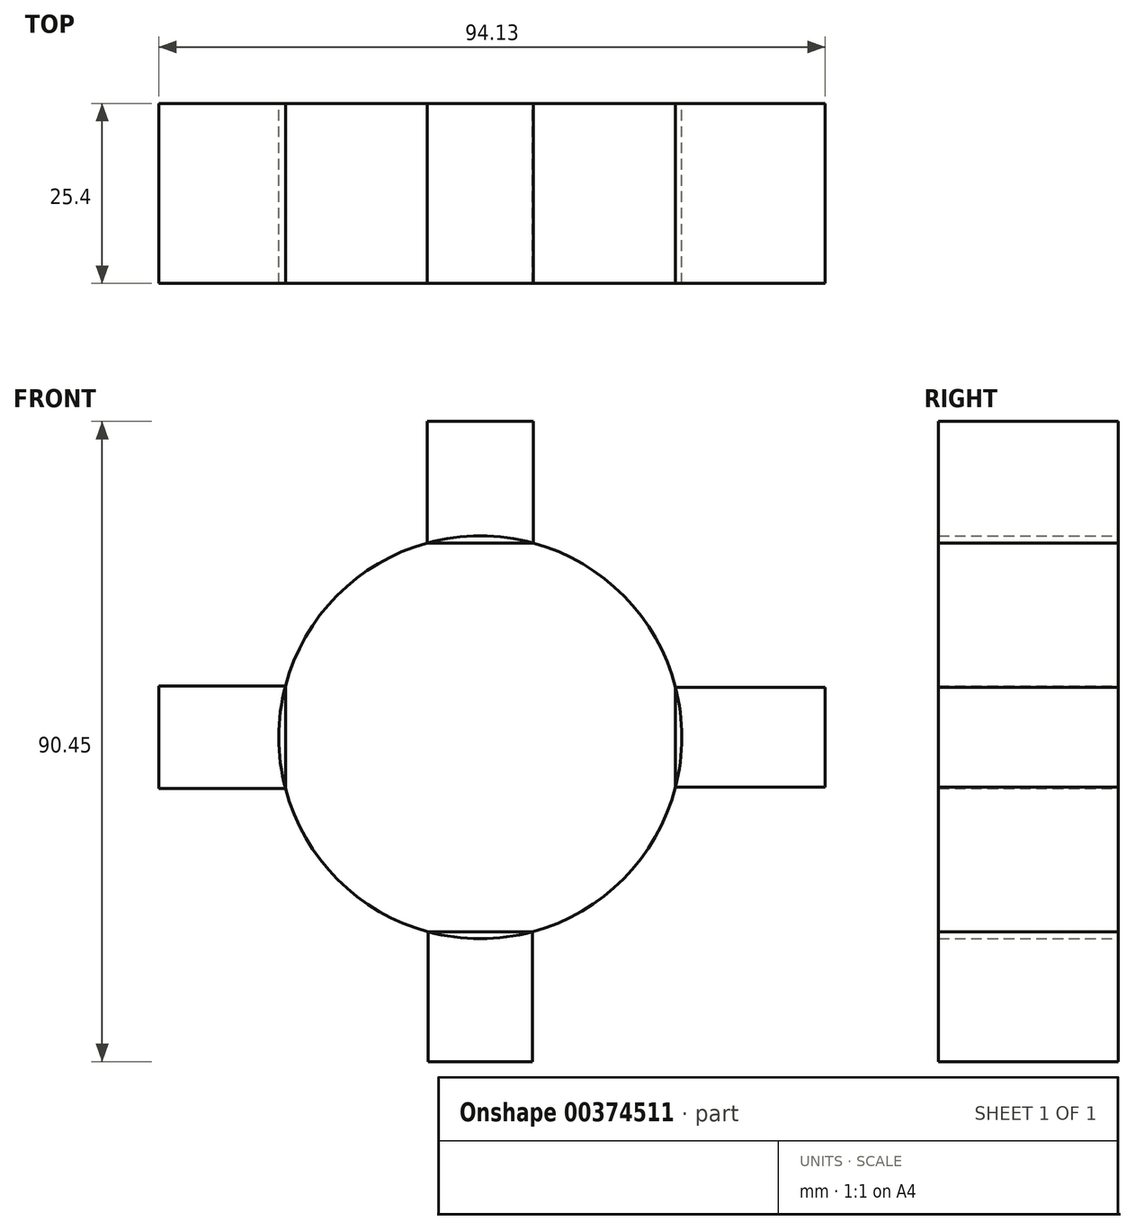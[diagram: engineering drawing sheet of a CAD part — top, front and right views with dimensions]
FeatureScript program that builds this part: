
annotation { "Feature Type Name" : "Feature", "Feature Type Description" : "" }
export const myFeature = defineFeature(function(context is Context, id is Id, definition is map)
    precondition{}
    {
        {
            var Q0;
            Q0=qCreatedBy(makeId("Front.planeOp"),FACE);
            var sketch = newSketch(context, id + "F0", { "sketchPlane" : qUnion([Q0])});
            skCircle(sketch, "E0", {"center": v(0, 0) * mm, "radius": 28.46 * mm});
            skLineSegment(sketch, "E1.bottom", {"start": v(-7.52, 27.45) * mm, "end": v(7.52, 27.45) * mm});
            skLineSegment(sketch, "E1.top", {"start": v(-7.52, 44.63) * mm, "end": v(7.52, 44.63) * mm});
            skLineSegment(sketch, "E1.left", {"start": v(-7.52, 27.45) * mm, "end": v(-7.52, 44.63) * mm});
            skLineSegment(sketch, "E1.right", {"start": v(7.52, 27.45) * mm, "end": v(7.52, 44.63) * mm});
            skPoint(sketch, "E1.middle", {"position": v(0, 36.04) * mm});
            skLineSegment(sketch, "E2.bottom", {"start": v(-7.34, -27.5) * mm, "end": v(7.34, -27.5) * mm});
            skLineSegment(sketch, "E2.top", {"start": v(-7.34, -45.82) * mm, "end": v(7.34, -45.82) * mm});
            skLineSegment(sketch, "E2.left", {"start": v(-7.34, -27.5) * mm, "end": v(-7.34, -45.82) * mm});
            skLineSegment(sketch, "E2.right", {"start": v(7.34, -27.5) * mm, "end": v(7.34, -45.82) * mm});
            skPoint(sketch, "E2.middle", {"position": v(0, -36.66) * mm});
            skLineSegment(sketch, "E3.bottom", {"start": v(-27.52, 7.24) * mm, "end": v(-45.4, 7.24) * mm});
            skLineSegment(sketch, "E3.top", {"start": v(-27.52, -7.24) * mm, "end": v(-45.4, -7.24) * mm});
            skLineSegment(sketch, "E3.left", {"start": v(-27.52, 7.24) * mm, "end": v(-27.52, -7.24) * mm});
            skLineSegment(sketch, "E3.right", {"start": v(-45.4, 7.24) * mm, "end": v(-45.4, -7.24) * mm});
            skPoint(sketch, "E3.middle", {"position": v(-36.46, 0) * mm});
            skLineSegment(sketch, "E4.bottom", {"start": v(27.57, 7.07) * mm, "end": v(48.73, 7.07) * mm});
            skLineSegment(sketch, "E4.top", {"start": v(27.57, -7.07) * mm, "end": v(48.73, -7.07) * mm});
            skLineSegment(sketch, "E4.left", {"start": v(27.57, 7.07) * mm, "end": v(27.57, -7.07) * mm});
            skLineSegment(sketch, "E4.right", {"start": v(48.73, 7.07) * mm, "end": v(48.73, -7.07) * mm});
            skPoint(sketch, "E4.middle", {"position": v(38.15, 0) * mm});
            skSolve(sketch);
        }
        {
            var Q0;
            Q0=makeQuery(id+"F0.imprint","IMPRINT",FACE,{"disambiguationData":[TD([[makeQuery(id+"F0.imprint","IMPRINT",EDGE,{"derivedFrom":sQuery(id+"F0.wireOp",EDGE,"E1.top")}),-1.0]])]});
            var Q1;
            {var subQ4=sQuery(id+"F0.wireOp",EDGE,"E1.bottom");Q1=makeQuery(id+"F0.imprint","IMPRINT",FACE,{"disambiguationData":[TD([[makeQuery(id+"F0.imprint","IMPRINT",EDGE,{"derivedFrom":subQ4}),-1.0]])]});}
            var Q2;
            {var subQ1=sQuery(id+"F0.wireOp",EDGE,"E4.bottom");Q2=makeQuery(id+"F0.imprint","IMPRINT",FACE,{"disambiguationData":[TD([[makeQuery(id+"F0.imprint","IMPRINT",EDGE,{"derivedFrom":subQ1}),-1.0]])]});}
            var Q3;
            Q3=makeQuery(id+"F0.imprint","IMPRINT",FACE,{"disambiguationData":[TD([[makeQuery(id+"F0.imprint","IMPRINT",EDGE,{"derivedFrom":sQuery(id+"F0.wireOp",EDGE,"E2.top")}),1.0]])]});
            var Q4;
            {var subQ1=sQuery(id+"F0.wireOp",EDGE,"E3.bottom");Q4=makeQuery(id+"F0.imprint","IMPRINT",FACE,{"disambiguationData":[TD([[makeQuery(id+"F0.imprint","IMPRINT",EDGE,{"derivedFrom":subQ1}),1.0]])]});}
            extrude(context, id + "F1", {"entities" : qUnion([Q0, Q1, Q2, Q3, Q4]), "depth" : 25.4 * mm});
        }
    });
